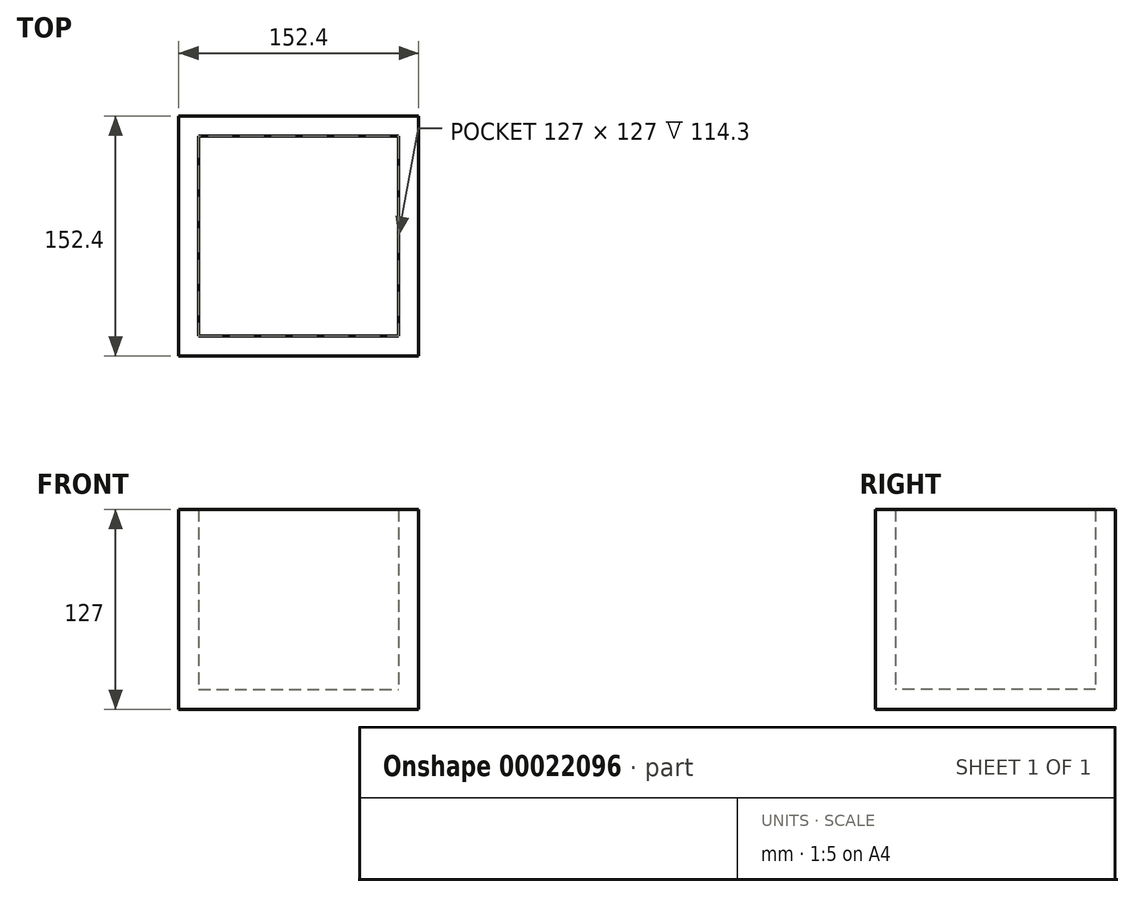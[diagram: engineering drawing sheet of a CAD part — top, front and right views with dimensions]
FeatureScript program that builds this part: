
annotation { "Feature Type Name" : "Feature", "Feature Type Description" : "" }
export const myFeature = defineFeature(function(context is Context, id is Id, definition is map)
    precondition{}
    {
        {
            var Q0;
            Q0=qCreatedBy(makeId("Top.planeOp"),FACE);
            var sketch = newSketch(context, id + "F0", { "sketchPlane" : qUnion([Q0])});
            skLineSegment(sketch, "E0.bottom", {"start": v(-28.66, 107.79) * mm, "end": v(123.74, 107.79) * mm});
            skLineSegment(sketch, "E0.top", {"start": v(-28.66, -44.61) * mm, "end": v(123.74, -44.61) * mm});
            skLineSegment(sketch, "E0.left", {"start": v(-28.66, 107.79) * mm, "end": v(-28.66, -44.61) * mm});
            skLineSegment(sketch, "E0.right", {"start": v(123.74, 107.79) * mm, "end": v(123.74, -44.61) * mm});
            skLineSegment(sketch, "E1.bottom", {"start": v(-28.66, -44.61) * mm, "end": v(22.14, -44.61) * mm});
            skLineSegment(sketch, "E1.top", {"start": v(-28.66, 107.79) * mm, "end": v(22.14, 107.79) * mm});
            skLineSegment(sketch, "E1.left", {"start": v(-28.66, -44.61) * mm, "end": v(-28.66, 107.79) * mm});
            skLineSegment(sketch, "E1.right", {"start": v(22.14, -44.61) * mm, "end": v(22.14, 107.79) * mm});
            skLineSegment(sketch, "E2.bottom", {"start": v(123.74, -44.61) * mm, "end": v(72.94, -44.61) * mm});
            skLineSegment(sketch, "E2.top", {"start": v(123.74, 107.79) * mm, "end": v(72.94, 107.79) * mm});
            skLineSegment(sketch, "E2.left", {"start": v(123.74, -44.61) * mm, "end": v(123.74, 107.79) * mm});
            skLineSegment(sketch, "E2.right", {"start": v(72.94, -44.61) * mm, "end": v(72.94, 107.79) * mm});
            skSolve(sketch);
        }
        {
            var Q0;
            Q0=makeQuery(id+"F0.imprint","IMPRINT",FACE,{"disambiguationData":[TD([[makeQuery(id+"F0.imprint","IMPRINT",EDGE,{"derivedFrom":sQuery(id+"F0.wireOp",EDGE,"E0.bottom")}),-1.0]])]});
            var Q1;
            Q1=makeQuery(id+"F0.imprint","IMPRINT",FACE,{"disambiguationData":[TD([[makeQuery(id+"F0.imprint","IMPRINT",EDGE,{"derivedFrom":sQuery(id+"F0.wireOp",EDGE,"E1.bottom")}),1.0]])]});
            var Q2;
            Q2=makeQuery(id+"F0.imprint","IMPRINT",FACE,{"disambiguationData":[TD([[makeQuery(id+"F0.imprint","IMPRINT",EDGE,{"derivedFrom":sQuery(id+"F0.wireOp",EDGE,"E2.bottom")}),-1.0]])]});
            extrude(context, id + "F1", {"entities" : qUnion([Q0, Q1, Q2]), "depth" : 127 * mm});
        }
        {
            var Q0;
            Q0=makeQuery(id+"F1.opExtrude","CAP_FACE",FACE,{"disambiguationData":[OSD([sQuery(id+"F0.wireOp",EDGE,"E0.bottom"),sQuery(id+"F0.wireOp",EDGE,"E0.top"),sQuery(id+"F0.wireOp",EDGE,"E0.left"),sQuery(id+"F0.wireOp",EDGE,"E0.right")])],"isStart":false});
            shell(context, id + "F2", {"entities" : qUnion([Q0]), "thickness" : 12.7 * mm});
        }
    });
